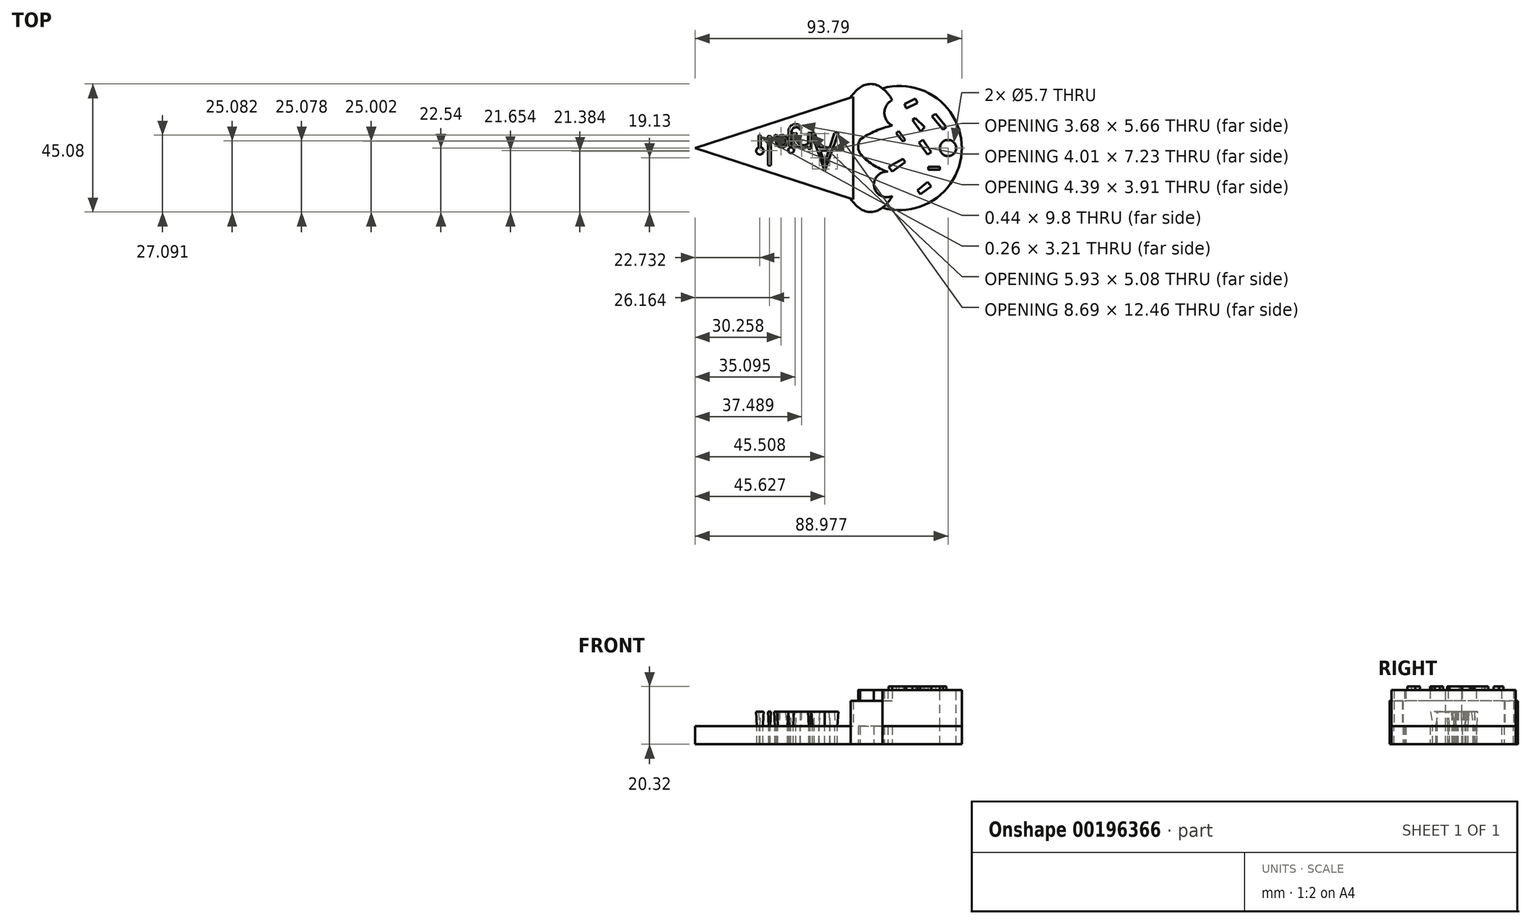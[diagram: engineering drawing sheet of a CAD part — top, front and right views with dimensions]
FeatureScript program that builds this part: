
annotation { "Feature Type Name" : "Feature", "Feature Type Description" : "" }
export const myFeature = defineFeature(function(context is Context, id is Id, definition is map)
    precondition{}
    {
        {
            var Q0;
            Q0=qCreatedBy(makeId("Top.planeOp"),FACE);
            var sketch = newSketch(context, id + "F0", { "sketchPlane" : qUnion([Q0])});
            skLineSegment(sketch, "E0", {"start": v(-55.55, 0) * mm, "end": v(0, 18.05) * mm});
            skLineSegment(sketch, "E1.MirrorCS", {"start": v(-55.55, 0) * mm, "end": v(0, -18.05) * mm});
            skLineSegment(sketch, "E2", {"start": v(0, 18.05) * mm, "end": v(0, -18.05) * mm});
            skEllipticalArc(sketch, "E3", {});
            skArc(sketch, "E4", {"start": v(13.8, -16.86) * mm, "mid": v(34.96, 0) * mm, "end": v(13.8, 16.86) * mm});
            skEllipticalArc(sketch, "E5.trimOffspring", {});
            skCircle(sketch, "E6", {"center": v(25.53, 0) * mm, "radius": 2.81 * mm});
            skArc(sketch, "E7", {"start": v(13.8, 16.86) * mm, "mid": v(11, 12.38) * mm, "end": v(13.8, 7.9) * mm});
            skArc(sketch, "E8", {"start": v(13.8, 7.9) * mm, "mid": v(7.9, 6) * mm, "end": v(2.46, 3) * mm});
            skArc(sketch, "E9", {"start": v(2.46, 3) * mm, "mid": v(1.79, 0.53) * mm, "end": v(2.46, -1.92) * mm});
            skArc(sketch, "E10", {"start": v(2.46, -1.92) * mm, "mid": v(7.6, -6.24) * mm, "end": v(13.8, -8.76) * mm});
            skArc(sketch, "E11", {"start": v(13.8, -8.76) * mm, "mid": v(7.35, -12.81) * mm, "end": v(13.8, -16.86) * mm});
            skLineSegment(sketch, "E12", {"start": v(27.67, 10.25) * mm, "end": v(22.75, 8.12) * mm});
            skLineSegment(sketch, "E13", {"start": v(25.53, -10.47) * mm, "end": v(22.75, -7.9) * mm});
            skLineSegment(sketch, "E14", {"start": v(18.68, 8.12) * mm, "end": v(15.97, 3) * mm});
            skLineSegment(sketch, "E15", {"start": v(15.97, -4.27) * mm, "end": v(11, 0) * mm});
            skLineSegment(sketch, "E16", {"start": v(17.66, -8.97) * mm, "end": v(15.97, -12.2) * mm});
            skLineSegment(sketch, "E17", {"start": v(22.75, -3.63) * mm, "end": v(18.68, -3.63) * mm});
            skLineSegment(sketch, "E18", {"start": v(-10.04, -6.24) * mm, "end": v(-8.2, -0.58) * mm});
            skPoint(sketch, "E18.startSnap0", {"position": v(7.6, -6.24) * mm});
            skLineSegment(sketch, "E19.MirrorCS", {"start": v(-10.04, -6.24) * mm, "end": v(-11.88, -0.58) * mm});
            skLineSegment(sketch, "E20", {"start": v(-15.6, 5.08) * mm, "end": v(-15.6, 1.55) * mm});
            skArc(sketch, "E21", {"start": v(-20.13, 3.31) * mm, "mid": v(-18.47, 0.88) * mm, "end": v(-15.6, 1.55) * mm});
            skLineSegment(sketch, "E22", {"start": v(-20.13, 3.31) * mm, "end": v(-20.13, 5.08) * mm});
            skPoint(sketch, "E23.end.orphan", {"position": v(-19.44, 5.08) * mm});
            skCircle(sketch, "E24", {"center": v(-21.8, -0.74) * mm, "radius": 0.75 * mm});
            skLineSegment(sketch, "E25", {"start": v(-21.88, 0.94) * mm, "end": v(-21.88, 5.74) * mm});
            skArc(sketch, "E26", {"start": v(-21.88, 5.74) * mm, "mid": v(-20.65, 7.47) * mm, "end": v(-18.6, 6.86) * mm});
            skArc(sketch, "E27", {"start": v(-26.47, 1.14) * mm, "mid": v(-23.1, 2.59) * mm, "end": v(-26.7, 3.27) * mm});
            skLineSegment(sketch, "E28", {"start": v(-26.47, 1.14) * mm, "end": v(-27.49, 4.14) * mm});
            skLineSegment(sketch, "E29", {"start": v(-29.17, -5.78) * mm, "end": v(-29.17, 3.98) * mm});
            skLineSegment(sketch, "E30", {"start": v(-32.69, 0.94) * mm, "end": v(-32.69, 4.14) * mm});
            skCircle(sketch, "E31", {"center": v(-32.77, -0.98) * mm, "radius": 1.04 * mm});
            skLineSegment(sketch, "E32", {"start": v(-8.01, 0) * mm, "end": v(-12.07, 0) * mm});
            skLineSegment(sketch, "E33", {"start": v(-6.37, 5.08) * mm, "end": v(-5.58, 5.08) * mm});
            skLineSegment(sketch, "E34", {"start": v(-5.58, 5.08) * mm, "end": v(-10.04, -7.39) * mm});
            skLineSegment(sketch, "E35", {"start": v(-10.04, -7.39) * mm, "end": v(-14.27, 5.08) * mm});
            skLineSegment(sketch, "E36", {"start": v(-14.27, 5.08) * mm, "end": v(-13.72, 5.08) * mm});
            skLineSegment(sketch, "E37", {"start": v(-8.2, -0.58) * mm, "end": v(-11.88, -0.58) * mm});
            skLineSegment(sketch, "E38.trimOffspring", {"start": v(-12.07, 0) * mm, "end": v(-13.72, 5.08) * mm});
            skLineSegment(sketch, "E39.trimOffspring", {"start": v(-8.01, 0) * mm, "end": v(-6.37, 5.08) * mm});
            skLineSegment(sketch, "E40", {"start": v(-15.6, 0) * mm, "end": v(-15.1, 0) * mm});
            skLineSegment(sketch, "E41", {"start": v(-15.1, 0) * mm, "end": v(-15.1, 5.08) * mm});
            skLineSegment(sketch, "E42", {"start": v(-15.1, 5.08) * mm, "end": v(-15.6, 5.08) * mm});
            skArc(sketch, "E43", {"start": v(-21.03, 3.31) * mm, "mid": v(-19, 0.57) * mm, "end": v(-15.6, 0.8) * mm});
            skLineSegment(sketch, "E44", {"start": v(-21.03, 3.31) * mm, "end": v(-21.03, 5) * mm});
            skLineSegment(sketch, "E45", {"start": v(-21.03, 5) * mm, "end": v(-20.13, 5.08) * mm});
            skLineSegment(sketch, "E46", {"start": v(-21.88, 0.94) * mm, "end": v(-22.35, 0.94) * mm});
            skLineSegment(sketch, "E47", {"start": v(-22.35, 0.94) * mm, "end": v(-22.46, 5.87) * mm});
            skArc(sketch, "E48", {"start": v(-18.45, 7.3) * mm, "mid": v(-20.97, 8.04) * mm, "end": v(-22.46, 5.87) * mm});
            skLineSegment(sketch, "E49", {"start": v(-18.6, 6.86) * mm, "end": v(-18.45, 7.3) * mm});
            skArc(sketch, "E50", {"start": v(-26.03, 1.29) * mm, "mid": v(-23.58, 2.86) * mm, "end": v(-26.49, 2.62) * mm});
            skLineSegment(sketch, "E51", {"start": v(-26.03, 1.29) * mm, "end": v(-26.49, 2.62) * mm});
            skLineSegment(sketch, "E52", {"start": v(-27.1, 4.42) * mm, "end": v(-27.49, 4.14) * mm});
            skLineSegment(sketch, "E53.trimOffspring", {"start": v(-26.7, 3.27) * mm, "end": v(-27.1, 4.42) * mm});
            skLineSegment(sketch, "E54", {"start": v(-29.17, -5.78) * mm, "end": v(-29.6, -5.78) * mm});
            skLineSegment(sketch, "E55", {"start": v(-29.6, -5.78) * mm, "end": v(-29.6, 4.01) * mm});
            skLineSegment(sketch, "E56", {"start": v(-29.6, 4.01) * mm, "end": v(-29.17, 3.98) * mm});
            skLineSegment(sketch, "E57", {"start": v(-32.69, 0.94) * mm, "end": v(-32.95, 0.94) * mm});
            skLineSegment(sketch, "E58", {"start": v(-32.95, 0.94) * mm, "end": v(-32.95, 4.15) * mm});
            skLineSegment(sketch, "E59", {"start": v(-32.95, 4.15) * mm, "end": v(-32.69, 4.14) * mm});
            skLineSegment(sketch, "E60", {"start": v(22.75, -3.63) * mm, "end": v(22.75, -4.36) * mm});
            skLineSegment(sketch, "E61", {"start": v(22.75, -4.36) * mm, "end": v(18.73, -4.36) * mm});
            skLineSegment(sketch, "E62", {"start": v(18.73, -4.36) * mm, "end": v(18.68, -3.63) * mm});
            skLineSegment(sketch, "E63", {"start": v(25.53, -10.47) * mm, "end": v(25.18, -10.85) * mm});
            skLineSegment(sketch, "E64", {"start": v(25.18, -10.85) * mm, "end": v(22.29, -8.18) * mm});
            skLineSegment(sketch, "E65", {"start": v(22.29, -8.18) * mm, "end": v(22.75, -7.9) * mm});
            skLineSegment(sketch, "E66", {"start": v(15.97, -12.2) * mm, "end": v(15.36, -11.88) * mm});
            skLineSegment(sketch, "E67", {"start": v(15.36, -11.88) * mm, "end": v(17.12, -8.5) * mm});
            skLineSegment(sketch, "E68", {"start": v(17.12, -8.5) * mm, "end": v(17.66, -8.97) * mm});
            skLineSegment(sketch, "E69", {"start": v(15.97, -4.27) * mm, "end": v(15.53, -4.79) * mm});
            skLineSegment(sketch, "E70", {"start": v(15.53, -4.79) * mm, "end": v(10.58, -0.53) * mm});
            skLineSegment(sketch, "E71", {"start": v(10.58, -0.53) * mm, "end": v(11, 0) * mm});
            skLineSegment(sketch, "E72", {"start": v(15.97, 3) * mm, "end": v(15.31, 3.34) * mm});
            skLineSegment(sketch, "E73", {"start": v(15.31, 3.34) * mm, "end": v(18.04, 8.52) * mm});
            skLineSegment(sketch, "E74", {"start": v(18.04, 8.52) * mm, "end": v(18.68, 8.12) * mm});
            skLineSegment(sketch, "E75", {"start": v(22.75, 8.12) * mm, "end": v(22.38, 8.97) * mm});
            skLineSegment(sketch, "E76", {"start": v(22.38, 8.97) * mm, "end": v(27.39, 11.15) * mm});
            skLineSegment(sketch, "E77", {"start": v(27.39, 11.15) * mm, "end": v(27.67, 10.25) * mm});
            skLineSegment(sketch, "E78.trimOffspring", {"start": v(-15.6, 0.8) * mm, "end": v(-15.6, 0) * mm});
            const initialGuessF0  = {"E3": [0.006195700261741877, 0, 0, 1, 0.02253953367471695, 0.011466819522103041, 2.4793557823544083, 3.867165584676997], "E5.trimOffspring": [0.006195700261741877, 0, 0, 1, 0.02253953367471695, 0.011466819522103041, 5.557612376092381, 0.6622368712353851]};
            skSetInitialGuess(sketch, initialGuessF0);
            skSolve(sketch);
        }
        {
            var Q0;
            {var subQ7=sQuery(id+"F0.wireOp",EDGE,"E2");Q0=makeQuery(id+"F0.imprint","IMPRINT",FACE,{"disambiguationData":[TD([[makeQuery(id+"F0.imprint","IMPRINT",EDGE,{"derivedFrom":subQ7}),-1.0]])]});}
            extrude(context, id + "F1", {"entities" : qUnion([Q0]), "oppositeDirection" : true, "depth" : 6.35 * mm});
        }
        {
            var Q0;
            {var subQ5=sQuery(id+"F0.wireOp",EDGE,"E2");Q0=makeQuery(id+"F0.imprint","IMPRINT",FACE,{"disambiguationData":[TD([[makeQuery(id+"F0.imprint","IMPRINT",EDGE,{"derivedFrom":subQ5}),1.0]])]});}
            extrude(context, id + "F2", {"entities" : qUnion([Q0]), "offsetDistance" : 25.4 * mm, "depth" : 8.9 * mm});
        }
        {
            var Q0;
            {var subQ5=sQuery(id+"F0.wireOp",EDGE,"E2");Q0=makeQuery(id+"F0.imprint","IMPRINT",FACE,{"disambiguationData":[TD([[makeQuery(id+"F0.imprint","IMPRINT",EDGE,{"derivedFrom":subQ5}),1.0]])]});}
            extrude(context, id + "F3", {"entities" : qUnion([Q0]), "operationType" : NewBodyOperationType.ADD, "oppositeDirection" : true, "depth" : 6.35 * mm});
        }
        {
            var Q0;
            Q0=makeQuery(id+"F0.imprint","IMPRINT",FACE,{"disambiguationData":[TD([[makeQuery(id+"F0.imprint","IMPRINT",EDGE,{"derivedFrom":sQuery(id+"F0.wireOp",EDGE,"E20")}),1.0]])]});
            var Q1;
            Q1=makeQuery(id+"F0.imprint","IMPRINT",FACE,{"disambiguationData":[TD([[makeQuery(id+"F0.imprint","IMPRINT",EDGE,{"derivedFrom":sQuery(id+"F0.wireOp",EDGE,"E18")}),-1.0]])]});
            var Q2;
            Q2=makeQuery(id+"F0.imprint","IMPRINT",FACE,{"disambiguationData":[TD([[makeQuery(id+"F0.imprint","IMPRINT",EDGE,{"derivedFrom":sQuery(id+"F0.wireOp",EDGE,"E25")}),1.0]])]});
            var Q3;
            Q3=makeQuery(id+"F0.imprint","IMPRINT",FACE,{"disambiguationData":[TD([[makeQuery(id+"F0.imprint","IMPRINT",EDGE,{"derivedFrom":sQuery(id+"F0.wireOp",EDGE,"E24")}),1.0]])]});
            var Q4;
            Q4=makeQuery(id+"F0.imprint","IMPRINT",FACE,{"disambiguationData":[TD([[makeQuery(id+"F0.imprint","IMPRINT",EDGE,{"derivedFrom":sQuery(id+"F0.wireOp",EDGE,"E27")}),1.0]])]});
            var Q5;
            Q5=makeQuery(id+"F0.imprint","IMPRINT",FACE,{"disambiguationData":[TD([[makeQuery(id+"F0.imprint","IMPRINT",EDGE,{"derivedFrom":sQuery(id+"F0.wireOp",EDGE,"E29")}),1.0]])]});
            var Q6;
            Q6=makeQuery(id+"F0.imprint","IMPRINT",FACE,{"disambiguationData":[TD([[makeQuery(id+"F0.imprint","IMPRINT",EDGE,{"derivedFrom":sQuery(id+"F0.wireOp",EDGE,"E31")}),1.0]])]});
            var Q7;
            Q7=makeQuery(id+"F0.imprint","IMPRINT",FACE,{"disambiguationData":[TD([[makeQuery(id+"F0.imprint","IMPRINT",EDGE,{"derivedFrom":sQuery(id+"F0.wireOp",EDGE,"E30")}),1.0]])]});
            extrude(context, id + "F4", {"entities" : qUnion([Q0, Q1, Q2, Q3, Q4, Q5, Q6, Q7]), "depth" : 5.08 * mm, "hasDraft" : true, "draftAngle" : 3 * degree});
        }
        {
            var Q0;
            Q0=makeQuery(id+"F0.imprint","IMPRINT",FACE,{"disambiguationData":[TD([[makeQuery(id+"F0.imprint","IMPRINT",EDGE,{"derivedFrom":sQuery(id+"F0.wireOp",EDGE,"E18")}),-1.0]])]});
            extrude(context, id + "F5", {"entities" : qUnion([Q0]), "oppositeDirection" : true, "depth" : 6.35 * mm});
        }
        {
            var Q0;
            Q0=qCreatedBy(makeId("Top.planeOp"),FACE);
            var sketch = newSketch(context, id + "F6", { "sketchPlane" : qUnion([Q0])});
            skArc(sketch, "E79", {"start": v(10.36, -21) * mm, "mid": v(38.24, 0) * mm, "end": v(10.36, 21) * mm});
            skEllipticalArc(sketch, "E80.0.0", {});
            skLineSegment(sketch, "E80.0.1", {"start": v(-0.86, 17.78) * mm, "end": v(0, 18.05) * mm});
            skLineSegment(sketch, "E80.0.2", {"start": v(0, 18.05) * mm, "end": v(0, -18.05) * mm});
            skLineSegment(sketch, "E80.0.3", {"start": v(0, -18.05) * mm, "end": v(-0.86, -17.78) * mm});
            skEllipticalArc(sketch, "E80.0.4", {});
            skArc(sketch, "E80.0.5", {"start": v(13.8, -16.86) * mm, "mid": v(7.42, -13.63) * mm, "end": v(12.23, -8.33) * mm});
            skArc(sketch, "E80.0.6", {"start": v(12.23, -8.33) * mm, "mid": v(6.9, -5.8) * mm, "end": v(2.46, -1.92) * mm});
            skArc(sketch, "E80.0.7", {"start": v(2.46, -1.92) * mm, "mid": v(1.79, 0.53) * mm, "end": v(2.46, 3) * mm});
            skArc(sketch, "E80.0.8", {"start": v(2.46, 3) * mm, "mid": v(7.9, 6) * mm, "end": v(13.8, 7.9) * mm});
            skArc(sketch, "E80.0.9", {"start": v(13.8, 7.9) * mm, "mid": v(11, 12.38) * mm, "end": v(13.8, 16.86) * mm});
            const initialGuessF6  = {"E80.0.0": [0.006195700261741877, 0, 0, 1, 0.02253953367471695, 0.011466819522103041, 5.557612376092381, 0.6622368712353852], "E80.0.4": [0.006195700261741877, 0, 0, 1, 0.02253953367471695, 0.011466819522103041, 2.4793557823544083, 3.8671655846769966]};
            skSetInitialGuess(sketch, initialGuessF6);
            skSolve(sketch);
        }
        {
            var Q0;
            {var subQ1=sQuery(id+"F6.wireOp",EDGE,"E79");Q0=makeQuery(id+"F6.imprint","IMPRINT",FACE,{"disambiguationData":[TD([[makeQuery(id+"F6.imprint","IMPRINT",EDGE,{"derivedFrom":subQ1}),1.0]])]});}
            extrude(context, id + "F7", {"entities" : qUnion([Q0]), "operationType" : NewBodyOperationType.ADD, "depth" : 12.7 * mm});
        }
        {
            var Q0;
            Q0=makeQuery(id+"F7.boolean.opBoolean","MERGE",FACE,{"derivedFrom":[makeQuery(id+"F2.opExtrude","CAP_FACE",FACE,{"disambiguationData":[OSD([sQuery(id+"F0.wireOp",EDGE,"E0"),sQuery(id+"F0.wireOp",EDGE,"E1.MirrorCS"),sQuery(id+"F0.wireOp",EDGE,"E2"),sQuery(id+"F0.wireOp",EDGE,"E3"),sQuery(id+"F0.wireOp",EDGE,"E5.trimOffspring"),sQuery(id+"F0.wireOp",EDGE,"E7"),sQuery(id+"F0.wireOp",EDGE,"E8"),sQuery(id+"F0.wireOp",EDGE,"E9"),sQuery(id+"F0.wireOp",EDGE,"E10"),sQuery(id+"F0.wireOp",EDGE,"E11")])],"isStart":true}),makeQuery(id+"F7.opExtrude","CAP_FACE",FACE,{"disambiguationData":[OSD([sQuery(id+"F6.wireOp",EDGE,"E79"),sQuery(id+"F6.wireOp",EDGE,"E80.0.0"),sQuery(id+"F6.wireOp",EDGE,"E80.0.4"),sQuery(id+"F6.wireOp",EDGE,"E80.0.5"),sQuery(id+"F6.wireOp",EDGE,"E80.0.6"),sQuery(id+"F6.wireOp",EDGE,"E80.0.7"),sQuery(id+"F6.wireOp",EDGE,"E80.0.8"),sQuery(id+"F6.wireOp",EDGE,"E80.0.9")])],"isStart":true})]});
            extrude(context, id + "F8", {"entities" : qUnion([Q0]), "depth" : 6.35 * mm});
        }
        {
            var Q0;
            Q0=makeQuery(id+"F7.opExtrude","CAP_FACE",FACE,{"disambiguationData":[OSD([sQuery(id+"F6.wireOp",EDGE,"E79"),sQuery(id+"F6.wireOp",EDGE,"E80.0.0"),sQuery(id+"F6.wireOp",EDGE,"E80.0.4"),sQuery(id+"F6.wireOp",EDGE,"E80.0.5"),sQuery(id+"F6.wireOp",EDGE,"E80.0.6"),sQuery(id+"F6.wireOp",EDGE,"E80.0.7"),sQuery(id+"F6.wireOp",EDGE,"E80.0.8"),sQuery(id+"F6.wireOp",EDGE,"E80.0.9")])],"isStart":false});
            var sketch = newSketch(context, id + "F9", { "sketchPlane" : qUnion([Q0])});
            skCircle(sketch, "E81", {"center": v(32.58, 0) * mm, "radius": 2.95 * mm});
            skLineSegment(sketch, "E82.bottom", {"start": v(30.58, -7.6) * mm, "end": v(26.53, -7.6) * mm});
            skLineSegment(sketch, "E82.top", {"start": v(30.58, -6.62) * mm, "end": v(26.53, -6.62) * mm});
            skLineSegment(sketch, "E82.left", {"start": v(30.58, -7.6) * mm, "end": v(30.58, -6.62) * mm});
            skLineSegment(sketch, "E82.right", {"start": v(26.53, -7.6) * mm, "end": v(26.53, -6.62) * mm});
            skLineSegment(sketch, "E83", {"start": v(27.47, -1.38) * mm, "end": v(26.27, -2.27) * mm});
            skLineSegment(sketch, "E84", {"start": v(26.27, -2.27) * mm, "end": v(23.19, 1.86) * mm});
            skLineSegment(sketch, "E85", {"start": v(23.19, 1.86) * mm, "end": v(24.52, 2.86) * mm});
            skLineSegment(sketch, "E86", {"start": v(24.52, 2.86) * mm, "end": v(27.47, -1.38) * mm});
            skLineSegment(sketch, "E87", {"start": v(26.27, -11.9) * mm, "end": v(27.47, -13.52) * mm});
            skLineSegment(sketch, "E88", {"start": v(27.47, -13.52) * mm, "end": v(23.73, -16.3) * mm});
            skLineSegment(sketch, "E89", {"start": v(23.73, -16.3) * mm, "end": v(22.65, -14.86) * mm});
            skLineSegment(sketch, "E90", {"start": v(22.65, -14.86) * mm, "end": v(26.27, -11.9) * mm});
            skLineSegment(sketch, "E91", {"start": v(17.52, -3.78) * mm, "end": v(18.36, -4.9) * mm});
            skLineSegment(sketch, "E92", {"start": v(18.36, -4.9) * mm, "end": v(16.06, -6.62) * mm});
            skLineSegment(sketch, "E93", {"start": v(16.06, -6.62) * mm, "end": v(13.8, -8.3) * mm});
            skLineSegment(sketch, "E94", {"start": v(13.8, -8.3) * mm, "end": v(12.56, -6.62) * mm});
            skLineSegment(sketch, "E95", {"start": v(12.56, -6.62) * mm, "end": v(17.52, -3.78) * mm});
            skLineSegment(sketch, "E96", {"start": v(18.36, 2.97) * mm, "end": v(17.52, 2.28) * mm});
            skLineSegment(sketch, "E97", {"start": v(17.52, 2.28) * mm, "end": v(15.12, 5.23) * mm});
            skLineSegment(sketch, "E98", {"start": v(15.12, 5.23) * mm, "end": v(16.06, 6) * mm});
            skLineSegment(sketch, "E99", {"start": v(16.06, 6) * mm, "end": v(18.36, 2.97) * mm});
            skLineSegment(sketch, "E100", {"start": v(32.82, 7.38) * mm, "end": v(31.68, 6.42) * mm});
            skLineSegment(sketch, "E101", {"start": v(31.68, 6.42) * mm, "end": v(27.77, 11.1) * mm});
            skLineSegment(sketch, "E102", {"start": v(27.77, 11.1) * mm, "end": v(28.95, 12.1) * mm});
            skLineSegment(sketch, "E103", {"start": v(28.95, 12.1) * mm, "end": v(32.82, 7.38) * mm});
            skLineSegment(sketch, "E104", {"start": v(21.9, 17.43) * mm, "end": v(22.66, 15.92) * mm});
            skLineSegment(sketch, "E105", {"start": v(22.66, 15.92) * mm, "end": v(18.78, 14) * mm});
            skLineSegment(sketch, "E106", {"start": v(18.78, 14) * mm, "end": v(18.03, 15.54) * mm});
            skLineSegment(sketch, "E107", {"start": v(18.03, 15.54) * mm, "end": v(21.9, 17.43) * mm});
            skLineSegment(sketch, "E108", {"start": v(25.2, 7.38) * mm, "end": v(23.78, 5.9) * mm});
            skLineSegment(sketch, "E109", {"start": v(23.78, 5.9) * mm, "end": v(20.9, 9.84) * mm});
            skLineSegment(sketch, "E110", {"start": v(20.9, 9.84) * mm, "end": v(21.9, 10.57) * mm});
            skLineSegment(sketch, "E111", {"start": v(21.9, 10.57) * mm, "end": v(25.2, 7.38) * mm});
            skSolve(sketch);
        }
        {
            var Q0;
            Q0=makeQuery(id+"F9.imprint","IMPRINT",FACE,{"disambiguationData":[TD([[makeQuery(id+"F9.imprint","IMPRINT",EDGE,{"derivedFrom":sQuery(id+"F9.wireOp",EDGE,"E83")}),-1.0]])]});
            var Q1;
            Q1=makeQuery(id+"F9.imprint","IMPRINT",FACE,{"disambiguationData":[TD([[makeQuery(id+"F9.imprint","IMPRINT",EDGE,{"derivedFrom":sQuery(id+"F9.wireOp",EDGE,"E82.bottom")}),-1.0]])]});
            var Q2;
            Q2=makeQuery(id+"F9.imprint","IMPRINT",FACE,{"disambiguationData":[TD([[makeQuery(id+"F9.imprint","IMPRINT",EDGE,{"derivedFrom":sQuery(id+"F9.wireOp",EDGE,"E87")}),-1.0]])]});
            var Q3;
            Q3=makeQuery(id+"F9.imprint","IMPRINT",FACE,{"disambiguationData":[TD([[makeQuery(id+"F9.imprint","IMPRINT",EDGE,{"derivedFrom":sQuery(id+"F9.wireOp",EDGE,"E91")}),-1.0]])]});
            var Q4;
            Q4=makeQuery(id+"F9.imprint","IMPRINT",FACE,{"disambiguationData":[TD([[makeQuery(id+"F9.imprint","IMPRINT",EDGE,{"derivedFrom":sQuery(id+"F9.wireOp",EDGE,"E96")}),-1.0]])]});
            var Q5;
            Q5=makeQuery(id+"F9.imprint","IMPRINT",FACE,{"disambiguationData":[TD([[makeQuery(id+"F9.imprint","IMPRINT",EDGE,{"derivedFrom":sQuery(id+"F9.wireOp",EDGE,"E108")}),-1.0]])]});
            var Q6;
            Q6=makeQuery(id+"F9.imprint","IMPRINT",FACE,{"disambiguationData":[TD([[makeQuery(id+"F9.imprint","IMPRINT",EDGE,{"derivedFrom":sQuery(id+"F9.wireOp",EDGE,"E104")}),-1.0]])]});
            var Q7;
            Q7=makeQuery(id+"F9.imprint","IMPRINT",FACE,{"disambiguationData":[TD([[makeQuery(id+"F9.imprint","IMPRINT",EDGE,{"derivedFrom":sQuery(id+"F9.wireOp",EDGE,"E100")}),-1.0]])]});
            extrude(context, id + "F10", {"entities" : qUnion([Q0, Q1, Q2, Q3, Q4, Q5, Q6, Q7]), "operationType" : NewBodyOperationType.ADD, "depth" : 1.27 * mm});
        }
        {
            var Q0;
            Q0=makeQuery(id+"F7.opExtrude","CAP_FACE",FACE,{"disambiguationData":[OSD([sQuery(id+"F6.wireOp",EDGE,"E79"),sQuery(id+"F6.wireOp",EDGE,"E80.0.0"),sQuery(id+"F6.wireOp",EDGE,"E80.0.4"),sQuery(id+"F6.wireOp",EDGE,"E80.0.5"),sQuery(id+"F6.wireOp",EDGE,"E80.0.6"),sQuery(id+"F6.wireOp",EDGE,"E80.0.7"),sQuery(id+"F6.wireOp",EDGE,"E80.0.8"),sQuery(id+"F6.wireOp",EDGE,"E80.0.9")])],"isStart":false});
            var sketch = newSketch(context, id + "F11", { "sketchPlane" : qUnion([Q0])});
            skCircle(sketch, "E112", {"center": v(33.43, 0) * mm, "radius": 2.85 * mm});
            skSolve(sketch);
        }
        {
            var Q0;
            Q0=makeQuery(id+"F11.imprint","IMPRINT",FACE,{"disambiguationData":[TD([[makeQuery(id+"F11.imprint","IMPRINT",EDGE,{"derivedFrom":sQuery(id+"F11.wireOp",EDGE,"E112")}),1.0]])]});
            extrude(context, id + "F12", {"entities" : qUnion([Q0]), "operationType" : NewBodyOperationType.REMOVE, "oppositeDirection" : true, "depth" : 25.4 * mm});
        }
    });
